# Revit family: LIXIL - 702805WH - VAAL DAISY WALL HUNG BASIN
name_source: partatom
category: Plumbing Fixtures
units: mm (PartAtom-declared; Revit-internal decimal feet)

## family parameters
Always vertical = Yes
Cut with Voids When Loaded = No
Enable Cutting in Views = No
Maintain Annotation Orientation = No
OmniClass Number = 23.45.00.00
OmniClass Title = Sanitary, Laundry, and Cleaning Equipment
Part Type = Normal
Room Calculation Point = No
Round Connector Dimension = Use Diameter
Shared = Yes
Work Plane-Based = No

## types (1)
- 702805WH
    CW Connection Diameter = 55 mm
    CW Connection Radius = 28 mm
    Default Elevation = 0 mm  [stored 0 ft]
    Description = Vaal Daisy 495mm(w) x 415mm(d) x 200mm(h) wall hung basin to detail and spec. See sanware schedule. Available from Lixil.
    Hosted on lixil.co.za = https://www.lixil.co.za
    M _ BASIN = M _ LIXIL - VAAL - PORCELAIN - WHITE 01
    M _ POP UP WASTE = M _ LIXIL - STAINLESS STEEL 01
    Product Specification = Supplier: Lixil.
Product Description: 
Vaal Daisy Round wall hung basin. Dimensions: 415mm long, 495mm wide, 200mm high. 3 X pre-punched tap holes. With overflow. Compatible with all Grohe/Cobra Original screw down taps and single lever mixers. 10 Year LIXIL Africa warranty. Access to Cobra TeamAssist technical team.
10 Year Warranty
Product Code: 1046390200.
SKU Code	: 702805WH.
Barcode: 	6005826072907.
Brand: Vaal.
Range: Daisy.
Category: Basins.
Sub-Category: Wall-hung.
Material: Ceramic.
Colour: White.
Product Height: 200 mm
Product Width: 495 mm
Product Length: 415  mm
Package Volume: 41085000 mm³.
Package Weight: 12.34 kg

Notes:
- Refer to manufacturer's and supplier's installation, maintenance and cleaning manual.
- Refer to manufacturer's and supplier's guarantees and warrantees document.
    Waste Connection Diameter = 102 mm
    Waste Connection Radius = 51 mm

note: [stored X ft] marks values corroborated as IEEE doubles in the binary element streams (Revit-internal decimal feet)

## geometry (parser evidence)
native form markers: Sweep x11
no freeform markers — native parametric forms only
